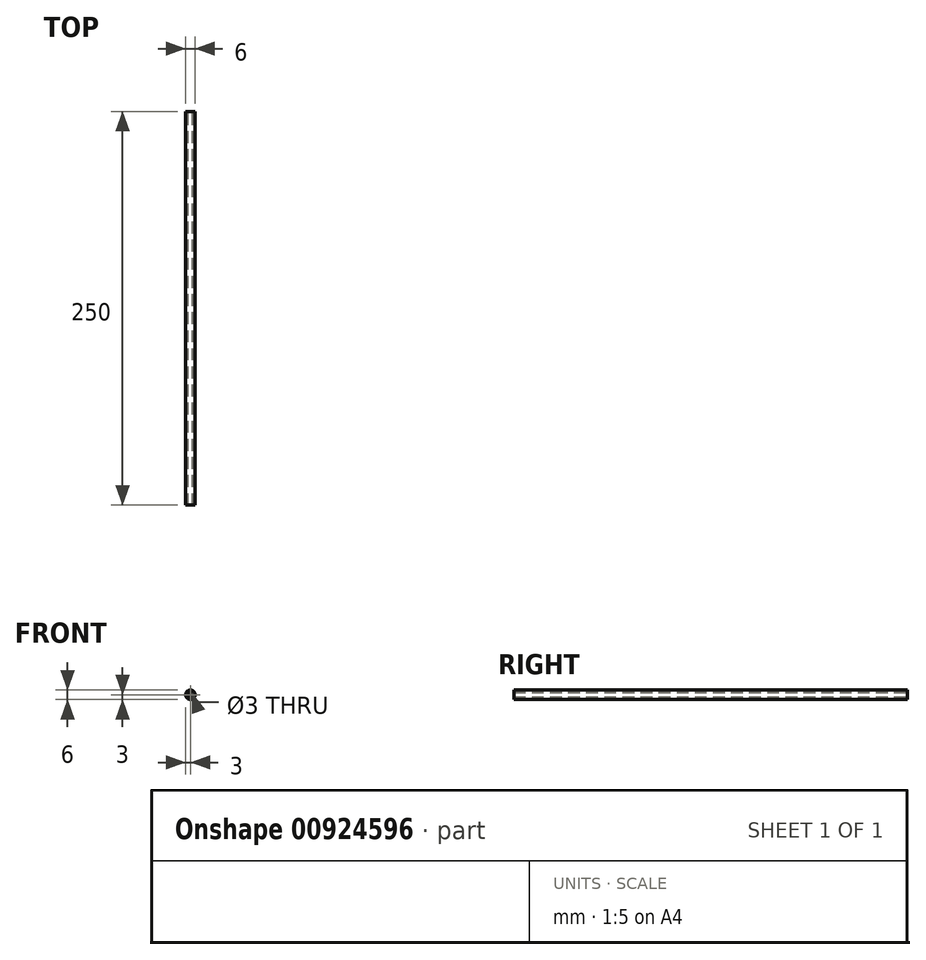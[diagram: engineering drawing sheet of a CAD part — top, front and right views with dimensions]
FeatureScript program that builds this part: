
annotation { "Feature Type Name" : "Feature", "Feature Type Description" : "" }
export const myFeature = defineFeature(function(context is Context, id is Id, definition is map)
    precondition{}
    {
        {
            var Q0;
            Q0=qCreatedBy(makeId("Front.planeOp"),FACE);
            var sketch = newSketch(context, id + "F0", { "sketchPlane" : qUnion([Q0])});
            skCircle(sketch, "E0", {"center": v(0, 0) * mm, "radius": 3 * mm});
            skCircle(sketch, "E1", {"center": v(0, 0) * mm, "radius": 1.5 * mm});
            skSolve(sketch);
        }
        {
            var Q0;
            Q0=makeQuery(id+"F0.imprint","IMPRINT",FACE,{"disambiguationData":[TD([[makeQuery(id+"F0.imprint","IMPRINT",EDGE,{"derivedFrom":sQuery(id+"F0.wireOp",EDGE,"E0")}),1.0]])]});
            extrude(context, id + "F1", {"entities" : qUnion([Q0]), "depth" : 250 * mm, "offsetDistance" : 25 * mm});
        }
    });
